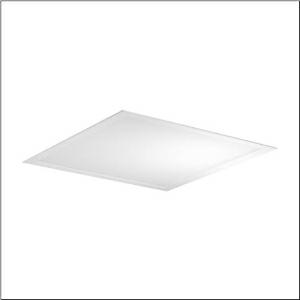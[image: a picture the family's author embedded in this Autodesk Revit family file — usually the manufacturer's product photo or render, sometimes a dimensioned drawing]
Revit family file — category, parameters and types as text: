
# Revit family: apollon_r__31_square_51mp11w72342_58c9
name_source: partatom
category: Lighting Fixtures
units: mm (PartAtom-declared; Revit-internal decimal feet)

## family parameters
Cut with Voids When Loaded = No
Host = Face
Light Source = No
Part Type = Normal
Room Calculation Point = No
Round Connector Dimension = Use Diameter
Shared = No

## types (1)
- Apollon® 31 square (1 x LED, 3800 lm, 27.5 W, 3000K)
    Apparent Load = 28 VA
    CIE Flux Codes = 61 87 97 100 100
    Color Rendering = 80
    Color Temperature = 3000K
    Default Elevation = 1800 mm
    Description = Apollon® 31 square, office luminaire, primary optical cover: micro prismatic cover, of PMMA, CAT 2 (L<= 3000cd/m²), light emission: direct distribution, primary light characteristic: symmetric, installation type: lay-in mounting, LED, rated luminous flux: 3.800lm, luminous efficacy: 138lm/W, light colour: 830, colour temperature: 3000K, control gear: ON/OFF, with terminal, 3-pole, mains connection: 220..240V, AC, 50/60Hz, rated input power: 28W, housing, of aluminium, traffic white (RAL 9016), module: M625, length: 620mm, width: 620mm, height: 62mm, recess depth: 180mm, housing upper side, of sheet steel, coated, protection rating (complete): IP20, protection rating (on room side): IP40, insulation class (complete): insulation class II (safety insulation), certification: CE, ENEC, impact resistance: IK03, permissible operating ambient temperature: -20..+40°C, permissible storage temperature: -20..+60°C, packaging unit: 1 piece
    Height = 0 mm  [stored 0 ft]
    Lamp = 1 x LED
    Lamp Light Flux = 3800 lm
    Lamp Power = 27.5 W
    Lamp count = 1
    Length = 620 mm
    Luminous efficacy = 138 lm/W
    Manufacturer = Siteco
    ModVariant = No
    Model = 51MP11W72342
    Mounting Place = Ceiling
    Mounting Type = Recessed
    Number of Poles = 1
    OnlyDefault = Yes
    Power Factor = 1
    Product Name = Apollon® 31 square
    Product group = office luminaire | ceiling recessed
    ProductGroupID = 400
    Protection Class = Protection class II
    Protection Degree = IP 20
    RLX_Detail_Level = 1
    RLX_Emergency_Light_Flux = 0 lm
    RLX_Emergency_Type = 0
    RLX_Emergency_Type_DB = No
    RlxData = <blob elided: 12981 chars, md5=40b1f53a>
    Socket = socket
    Standby Power = 0 W
    System Light Flux = 3800 lm
    System Power = 28 W
    Type Comments = Product without accessories
    Type Image = l_1291039.jpg
    URL = http://relux.com
    VarID = ---
    Voltage = 0 V
    Weight = 0.00 kg
    Width = 620 mm

note: [stored X ft] marks values corroborated as IEEE doubles in the binary element streams (Revit-internal decimal feet)

## geometry (parser evidence)
native form markers: Sweep x10
no freeform markers — native parametric forms only
